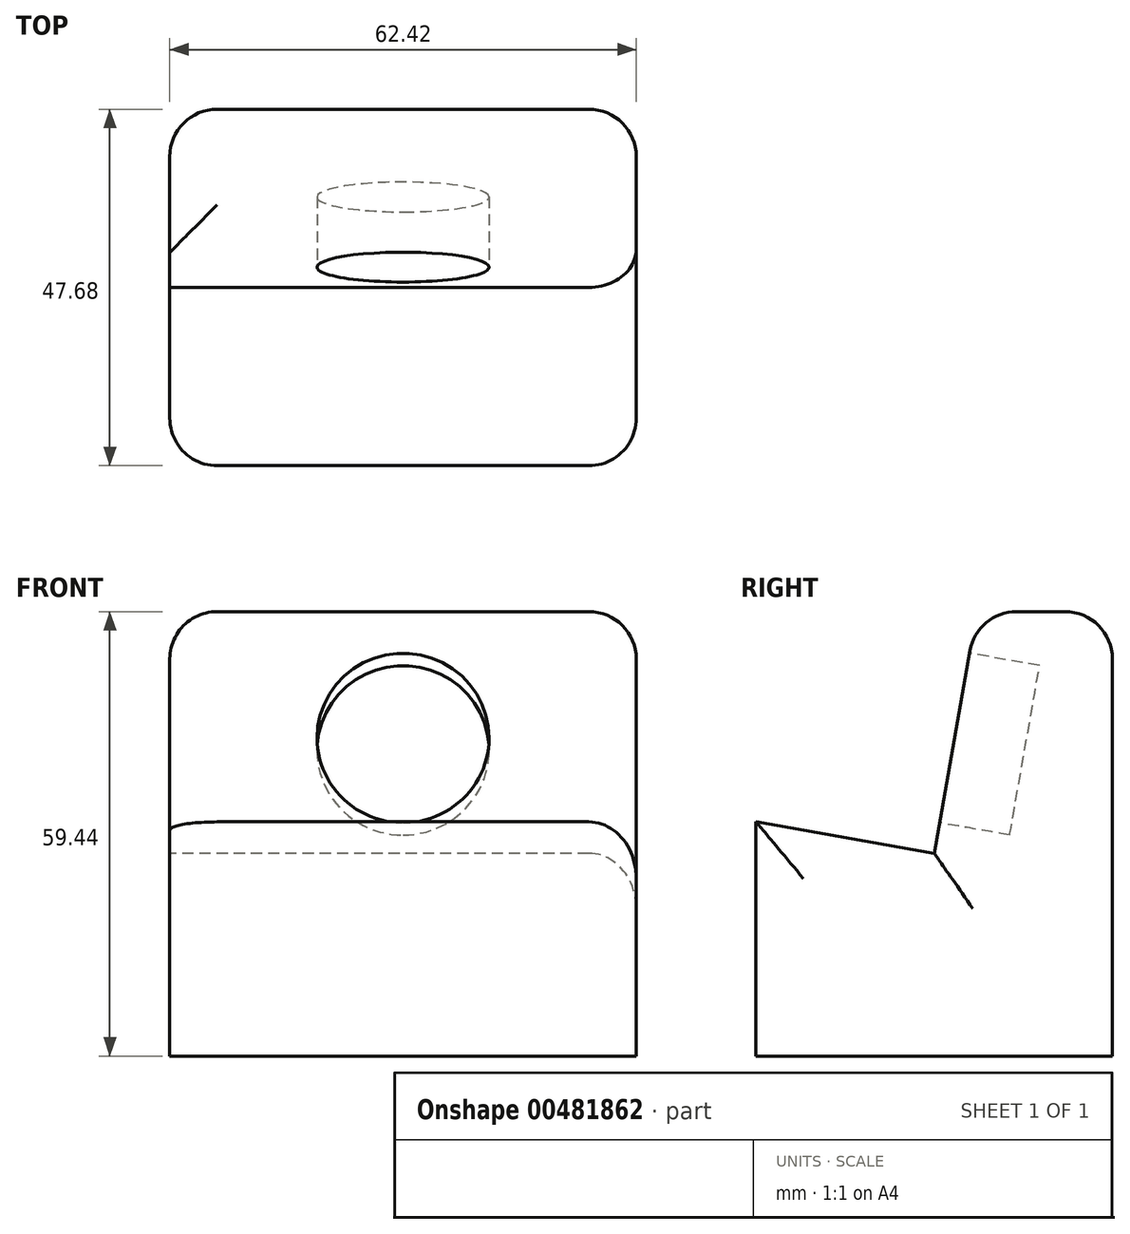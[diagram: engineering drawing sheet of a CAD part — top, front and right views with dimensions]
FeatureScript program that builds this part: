
annotation { "Feature Type Name" : "Feature", "Feature Type Description" : "" }
export const myFeature = defineFeature(function(context is Context, id is Id, definition is map)
    precondition{}
    {
        {
            var Q0;
            Q0=qCreatedBy(makeId("Top.planeOp"),FACE);
            var sketch = newSketch(context, id + "F0", { "sketchPlane" : qUnion([Q0])});
            skLineSegment(sketch, "E0.bottom", {"start": v(-31.2, 23.84) * mm, "end": v(31.2, 23.84) * mm});
            skLineSegment(sketch, "E0.top", {"start": v(-31.2, -23.84) * mm, "end": v(31.2, -23.84) * mm});
            skLineSegment(sketch, "E0.left", {"start": v(-31.2, 23.84) * mm, "end": v(-31.2, -23.84) * mm});
            skLineSegment(sketch, "E0.right", {"start": v(31.2, 23.84) * mm, "end": v(31.2, -23.84) * mm});
            skSolve(sketch);
        }
        {
            var Q0;
            Q0=makeQuery(id+"F0.imprint","IMPRINT",FACE,{"disambiguationData":[TD([[makeQuery(id+"F0.imprint","IMPRINT",EDGE,{"derivedFrom":sQuery(id+"F0.wireOp",EDGE,"E0.bottom")}),-1.0]])]});
            extrude(context, id + "F1", {"entities" : qUnion([Q0]), "depth" : 59.44 * mm});
        }
        {
            var Q0;
            Q0=makeQuery(id+"F1.opExtrude","SWEPT_FACE",FACE,{"disambiguationData":[OSD([sQuery(id+"F0.wireOp",EDGE,"E0.left")])]});
            var sketch = newSketch(context, id + "F2", { "sketchPlane" : qUnion([Q0])});
            skLineSegment(sketch, "E1", {"start": v(-5.7, 59.44) * mm, "end": v(0, 27.11) * mm});
            skLineSegment(sketch, "E2", {"start": v(0, 27.11) * mm, "end": v(23.84, 31.31) * mm});
            skLineSegment(sketch, "E3", {"start": v(23.84, 31.31) * mm, "end": v(23.84, 59.44) * mm});
            skLineSegment(sketch, "E4", {"start": v(23.84, 59.44) * mm, "end": v(-5.7, 59.44) * mm});
            skSolve(sketch);
        }
        {
            var Q0;
            Q0 = qSketchRegion(id + "F2", true);
            extrude(context, id + "F3", {"entities" : qUnion([Q0]), "operationType" : NewBodyOperationType.REMOVE, "endBound" : BoundingType.THROUGH_ALL, "oppositeDirection" : true, "depth" : 25.4 * mm});
        }
        {
            var Q0;
            Q0=makeQuery(id+"F3.boolean.opBoolean","COPY",FACE,{"derivedFrom":makeQuery(id+"F3.opExtrude","SWEPT_FACE",FACE,{"disambiguationData":[OSD([sQuery(id+"F2.wireOp",EDGE,"E1")])]})});
            var sketch = newSketch(context, id + "F4", { "sketchPlane" : qUnion([Q0])});
            skCircle(sketch, "E5", {"center": v(0, 42.36) * mm, "radius": 11.5 * mm});
            skSolve(sketch);
        }
        {
            var Q0;
            Q0 = qSketchRegion(id + "F4", true);
            extrude(context, id + "F5", {"entities" : qUnion([Q0]), "operationType" : NewBodyOperationType.REMOVE, "oppositeDirection" : true, "depth" : 9.52 * mm});
        }
        {
            var Q0;
            Q0=makeQuery(id+"F1.opExtrude","CAP_FACE",FACE,{"disambiguationData":[OSD([sQuery(id+"F0.wireOp",EDGE,"E0.bottom"),sQuery(id+"F0.wireOp",EDGE,"E0.top"),sQuery(id+"F0.wireOp",EDGE,"E0.left"),sQuery(id+"F0.wireOp",EDGE,"E0.right")])],"isStart":false});
            var Q1;
            Q1=makeQuery(id+"F1.opExtrude","SWEPT_EDGE",EDGE,{"disambiguationData":[OSD([sQuery(id+"F0.wireOp",EDGE,"E0.top"),sQuery(id+"F0.wireOp",EDGE,"E0.left")])]});
            var Q2;
            Q2=makeQuery(id+"F1.opExtrude","SWEPT_EDGE",EDGE,{"disambiguationData":[OSD([sQuery(id+"F0.wireOp",EDGE,"E0.top"),sQuery(id+"F0.wireOp",EDGE,"E0.right")])]});
            var Q3;
            Q3=makeQuery(id+"F3.boolean.opBoolean","COPY",EDGE,{"derivedFrom":makeQuery(id+"F3.opExtrude","SWEPT_EDGE",EDGE,{"disambiguationData":[OSD([sQuery(id+"F0.wireOp",EDGE,"E0.top"),sQuery(id+"F0.wireOp",EDGE,"E0.left"),sQuery(id+"F2.wireOp",EDGE,"E2"),sQuery(id+"F2.wireOp",EDGE,"E3")])]})});
            var Q4;
            Q4=makeQuery(id+"F3.boolean.opBoolean","COPY",EDGE,{"derivedFrom":makeQuery(id+"F3.opExtrude","CAP_EDGE",EDGE,{"disambiguationData":[OSD([sQuery(id+"F2.wireOp",EDGE,"E2")])],"isStart":true})});
            var Q5;
            Q5=makeQuery(id+"F3.boolean.opBoolean","COPY",EDGE,{"derivedFrom":makeQuery(id+"F3.opExtrude","CAP_EDGE",EDGE,{"disambiguationData":[OSD([sQuery(id+"F2.wireOp",EDGE,"E1")])],"isStart":true})});
            var Q6;
            Q6=makeQuery(id+"F3.boolean.opBoolean","INTERSECT",EDGE,{"derivedFrom":[makeQuery(id+"F1.opExtrude","SWEPT_FACE",FACE,{"disambiguationData":[OSD([sQuery(id+"F0.wireOp",EDGE,"E0.right")])]}),makeQuery(id+"F3.opExtrude","SWEPT_FACE",FACE,{"disambiguationData":[OSD([sQuery(id+"F2.wireOp",EDGE,"E2")])]})]});
            var Q7;
            Q7=makeQuery(id+"F3.boolean.opBoolean","INTERSECT",EDGE,{"derivedFrom":[makeQuery(id+"F1.opExtrude","SWEPT_FACE",FACE,{"disambiguationData":[OSD([sQuery(id+"F0.wireOp",EDGE,"E0.right")])]}),makeQuery(id+"F3.opExtrude","SWEPT_FACE",FACE,{"disambiguationData":[OSD([sQuery(id+"F2.wireOp",EDGE,"E1")])]})]});
            var Q8;
            Q8=makeQuery(id+"F1.opExtrude","SWEPT_EDGE",EDGE,{"disambiguationData":[OSD([sQuery(id+"F0.wireOp",EDGE,"E0.bottom"),sQuery(id+"F0.wireOp",EDGE,"E0.right")])]});
            var Q9;
            Q9=makeQuery(id+"F1.opExtrude","SWEPT_EDGE",EDGE,{"disambiguationData":[OSD([sQuery(id+"F0.wireOp",EDGE,"E0.bottom"),sQuery(id+"F0.wireOp",EDGE,"E0.left")])]});
            fillet(context, id + "F6", {"entities" : qUnion([Q0, Q1, Q2, Q3, Q4, Q5, Q6, Q7, Q8, Q9]), "radius" : 6.35 * mm, "tangentPropagation" : true, "allowEdgeOverflow" : false});
        }
    });
